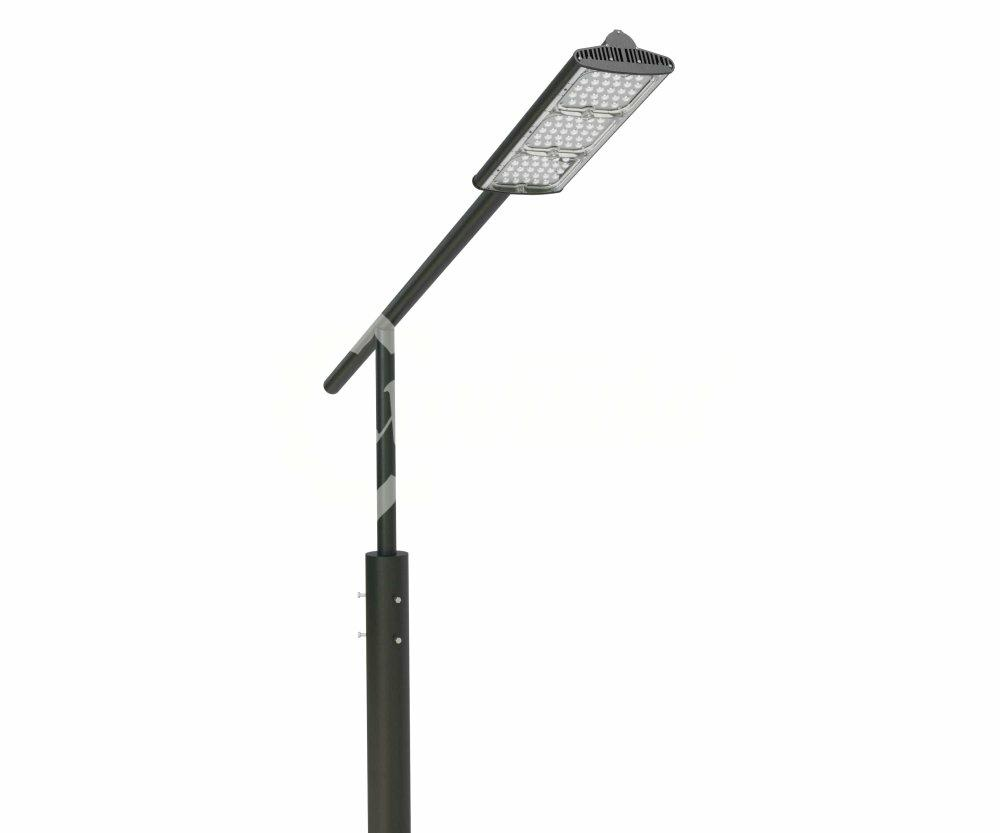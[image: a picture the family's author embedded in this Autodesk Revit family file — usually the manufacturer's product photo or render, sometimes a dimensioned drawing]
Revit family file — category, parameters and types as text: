
# Revit family: 10230 Стальной фонарный столб «Модерн-Э» со светильником Хоббика
name_source: partatom
category: Антураж
revit_build: Autodesk Revit 2018 (Build: 20180423_1000(x64)
units: mm (PartAtom-declared; Revit-internal decimal feet)

## family parameters
Всегда вертикально = Да
Источник визуального образа = Геометрия семейства
На основе рабочей плоскости = Нет
Общий = Нет
При загрузке вырезать с полостями = Нет
Точка расчета площади = Нет

## types (4) — shared parameters
URL = https://hobbyka.ru
Артикул товара = Арт. 10230
Группа модели = Светильники со стальными опорами
Длина = 1582 мм
Изготовитель = ООО «Хоббика»
Изображение типоразмера = Стальной фонарный столб «Модерн-Э» со светильником Арт 10230.jpg
Материал изделия = Сталь
Цвет каркаса = Сталь
Ширина = 203 мм

## per-type parameters (varying)
| type | Версия 3,6 м (80 Вт) | Версия 4,6 м (120 Вт) | Версия 5,6 м (120 Вт) | Версия 6,6 м (160 Вт) | Высота | Описание |
| Версия 3,6 м (80 Вт) | Да | Нет | Нет | Нет | 3600 мм | Стальной фонарный столб «Модерн-Э» со светильником. Версия 3,6 м (80 Вт) |
| Версия 4,6 м (120 Вт) | Нет | Да | Нет | Нет | 4600 мм | Стальной фонарный столб «Модерн-Э» со светильником. Версия 4,6 м (120 Вт) |
| Версия 5,6 м (120 Вт) | Нет | Нет | Да | Нет | 5600 мм | Стальной фонарный столб «Модерн-Э» со светильником. Версия 5,6 м (120 Вт) |
| Версия 6,6 м (160 Вт) | Нет | Нет | Нет | Да | 6600 мм | Стальной фонарный столб «Модерн-Э» со светильником. Версия 6,6 м (160 Вт) |
